# Revit family: toilets-hansgrohe-62020XXX-EluPura S Wall hung WC 540 rimless, HygieneEffect
name_source: partatom
category: Sanitärinstallationen
units: mm (PartAtom-declared; Revit-internal decimal feet)

## family parameters
Arbeitsebenenbasiert = Nein
Beim Laden mit Abzugskörper schneiden = Nein
Bemaßung runder Anschluss = Durchmesser verwenden
Beschriftungsausrichtung beibehalten = Nein
Gemeinsam genutzt = Ja
Immer vertikal = Ja
OmniClass-Nummer = 23.45.00.00
OmniClass-Titel = Sanitary, Laundry, and Cleaning Equipment
Raumberechnungspunkt = Nein
Teiletyp = Ventil - Zerlegung in

## types (2) — shared parameters
60193-60193450-GLOSSY_WHITE-200_RX0RY0RZ0TX0TY0TZ0_V = Nein
60193-60193450-GLOSSY_WHITE-400_RX0RY0RZ0TX0TY0TZ0_V = Nein
ARTNR = 62020450
BASENUMBER = 62020
BIMOBJECT = Sanitary: Toilets
CATALOG = Hansgrohe
CNSPipeRound/CP_Outlet_V = Nein
CNSPipeRound/CP_inlet_V = Nein
COLLECTION = toilets
COLLECTIONSET = EluPura S
DEPTH = 540
DESIGN = Germany
GTINCODE = 4059625479704
HEIGHT = 400
Hersteller = Hansgrohe
IDNR = 2
IFC = Furnishing element
NAME = EluPura S Wall hung WC 540 rimless, HygieneEffect
NBSYN = $BASENUMBER.-$ARTNR.-$SURFACE.-$LODLEVEL.
NN = EluPura S Wall hung WC 540 rimless
OBJECTTYPE = Object (single object)
OMNICLASS = 23-31 19 00 | Toilets
PERMALINK = 62020XXX
PRODUCTURL = https://pro.hansgrohe.com
REGIONSET = Worldwide
SPECIFICATION = Surfaces:  - 62020450 White   Specification:  • material: ceramic  • HygieneEffect - reduces the spread of coliform bacteria and salmonella (Escherichia coli ATCC8739/Salmonella enterica ATCC 13076. Test: ISO 22196: 2011-08) • Made to fit NoiseReduction: customized soundproofing mat included • degree of gloss: glossy  • flushing type: wash-down  • rimless • concealed fastening • horizontal outlet • installation type: wall-mounted
SURFACE = GLOSSY_WHITE
UNICLASS2015 = Pr_40_20_93_94 | WC pans
UNICLASS_2015_CODE = 40_20_93_94
WEIGHT = 22
WIDTH = 360
zero-valued in all types: Vorgabe-Ansicht

## per-type parameters (varying)
| type | 62020-62020450-GLOSSY_WHITE-200_RX0RY0RZ0TX0TY0TZ0_V | 62020-62020450-GLOSSY_WHITE-400_RX0RY0RZ0TX0TY0TZ0_V | LODLEVEL |
| 62020-62020450-GLOSSY_WHITE-200 | Ja | Nein | 200 |
| 62020-62020450-GLOSSY_WHITE-400 | Nein | Ja | 400 |

note: column(s) folded — value = type name in every type: LINA, Modell, NB

## geometry (parser evidence)
native form markers: Sweep x22
no freeform markers — native parametric forms only
